# Revit family: PGL8_Wall_Mount
name_source: partatom
category: Lighting Fixtures
units: mm (PartAtom-declared; Revit-internal decimal feet)

## family parameters
Cut with Voids When Loaded = No
Host = Face
Light Source = Yes
OmniClass Number = 23.80.70.00
OmniClass Title = Lighting
Part Type = Normal
Room Calculation Point = No
Round Connector Dimension = Use Diameter
Shared = No

## types (1)
- PGL8_Wall_Mount
    Assembly Code = D5020200
    Certifications = UL listed
    Color Filter = 16777215
    Default Elevation = 48 "
    Description = The legacy of the PGL continues with the PGL8 edge-lit with drop lens. The PGL8 provides effective solutions for meeting the dynamics and challenges of parking garage applications including IES recommendations. The drop lens reduces glare providing exceptional visual comfort and performance, making the PGL8 the ideal solution for parking garage and canopy applications.
    Dimming Interface = 0-10V
    Dimming Lamp Color Temperature Shift = <None>
    Distribution = Type V Concentrated, Type V Square, Type V Rectangular, Asymmetric
    Emit Shape Visible in Rendering = No
    Emit from Circle Diameter = 14 "
    Features = Patent pending edge-lit, drop lens optic
• The PGL8 offers exceptional uniformity and visual comfort with four
standard distribution patterns
• Multiple control options available for an intelligent parking garage
lighting solution
• Integral sensors, battery backup and uplight
    Glass = Paint - Matte White
    Housing = Paint -  Basic Black Textured
    IP Rating = IP 65
    Lamp = LED
    Manufacturer = KIM LIGHTING
    Model = PGL8
    Photometric Web File = PGL8-5C-128L-110-3K7.ies
    Power Factor = 0.90
    Tilt Angle = -90.00°
    Type Comments = Light Fixture
    URL = https://www.currentlighting.com
    Warranty = 5 Years Limited Warranty
    Width = 8.85 "

## geometry (parser evidence)
native form markers: Sweep x2
no freeform markers — native parametric forms only
